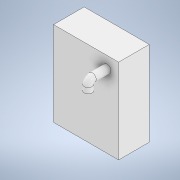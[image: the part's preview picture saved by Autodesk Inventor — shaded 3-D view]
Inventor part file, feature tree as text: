
AUTODESK INVENTOR PART (.ipt)
format: ipt  version: 2022 (Build 260153000, 153)  size: 124,928 bytes
history: native  units: in
note: dims shown in document units (in); Inventor stores cm internally (conversion verified against a paired STEP export)
features: sketch x4, extrude x3, plane x2, revolve x1
ambient origin geometry x8: Origin, YZ Plane, XZ Plane, XY Plane, X Axis, Y Axis, Z Axis, Center Point
bodies: Solid1 (feature_tree)
feature tree (10):
  extrude  "Extrusion1"  Depth=22.125in
  extrude  "Extrusion2"  Depth=8.0in
  plane  "Work Plane1"
  extrude  "Extrusion3"  Depth=3.0in
  plane  "Work Plane2"
  sketch  "Sketch5"  dims[d7=3.86in d8=0.0in d9=-4.069in d10=1.45in d11=0.0in d12=-3.0in d16=1.1in d17=90.0deg]
  revolve  "Revolution1"  [1 undecoded]
  sketch  "Sketch1"  dims[d0=17.0in d1=22.125in]
  sketch  "Sketch2"  dims[d2=8.0in d3=0.0in d4=2.0in]
  sketch  "Sketch3"  dims[d5=19.156in d6=3.0in]
note: 1 required parameter value undecoded (feature->parameter linkage not recoverable at this tier; creation-order binding heuristic only, values carry confidence <= 0.55)
